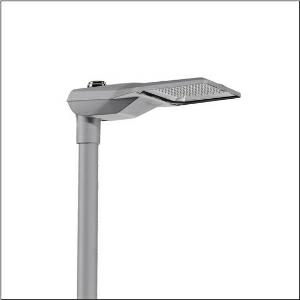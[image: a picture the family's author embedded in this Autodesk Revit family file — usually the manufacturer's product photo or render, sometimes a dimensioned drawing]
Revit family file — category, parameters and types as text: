
# Revit family: streetlight_sl_21_midi___st1_5a_5xe7p47n08mb_d352
name_source: partatom
category: Lighting Fixtures
units: mm (PartAtom-declared; Revit-internal decimal feet)

## family parameters
Cut with Voids When Loaded = No
Host = Face
Light Source = No
Part Type = Normal
Room Calculation Point = No
Round Connector Dimension = Use Diameter
Shared = No

## types (1)
- --- (1 x LED, 19830 lm, 147 W, 4000K)
    Apparent Load = 147 VA
    CIE Flux Codes = 22 53 95 100 100
    Color Rendering = 70
    Color Temperature = 4000K
    Default Elevation = 1800 mm
    Description = Streetlight SL 21 midi, mast luminaire, primary light control with lens, of PMMA, primary optical cover: cover, of toughened safety glass, transparent, light distribution: ST1.5a, light emission: direct distribution, primary light characteristic: asymmetric, installation type: side-entry, LED, 3G 2.5mm², High Power LED, rated luminous flux: 19.830lm, luminous efficacy: 135lm/W, light colour: 740, colour temperature: 4000K, control gear: NEMA (7pin), control: overheat protection, pre-setting: linear dimming characteristic, constant luminous flux control, time-dependent luminous flux control, flexible luminous flux parameterisation, mains connection: 220..240V, AC, 50/60Hz, connection cable pre-assembled, cable length: 12,5m, wiring characteristics: H05VV-F, start of lifetime: 147W, end of service life: 155W, reduction: 65W, luminaire housing, of diecast aluminium (EN AC-44300), powder-coated, Siteco® metallic grey (DB 702S), corrosivity category C5 mid according to DIN EN ISO 12944, multi-level sealing system, sealing non-destructively replaceable, inclination adjustable: 0°, 5°, 10°, 15°, length: 644mm, width: 335mm, height: 110mm, spigot size: 42mm (side-entry), mounting height: 4..8m, protection rating (complete): IP66, insulation class (complete): insulation class I (protective earthing), certification: CE, ENEC, ENEC+, VDE, impact resistance: IK10, permissible operating ambient temperature for outdoor applications: -40..+50°C, standard-compliant lighting for roads and squares, packaging unit: 1 piece

Light Distribution: ST1.5a
    Height = 111 mm
    Lamp = 1 x LED
    Lamp Light Flux = 19830 lm
    Lamp Power = 147 W
    Lamp count = 1
    Length = 644 mm
    Luminous efficacy = 135 lm/W
    Manufacturer = Siteco
    ModVariant = No
    Model = 5XE7P47N08MB
    Number of Poles = 1
    OnlyDefault = Yes
    Power Factor = 1
    Product Name = Streetlight SL 21 midi | ST1.5a
    Product group = mast luminaire | pylon top
    ProductGroupID = 6100
    Protection Class = Protection class I
    Protection Degree = IP 66
    RLX_Detail_Level = 1
    RLX_Emergency_Light_Flux = 0 lm
    RLX_Emergency_Type = 0
    RLX_Emergency_Type_DB = No
    RlxData = <blob elided: 30073 chars, md5=d4ea3021>
    Socket = socket
    Standby Power = 0 W
    System Light Flux = 19830 lm
    System Power = 147 W
    Type Comments = factory setting: luminous flux: 100 % | dim-lin: 254 | 750 mA
    Type Image = l_1294377.jpg
    URL = http://relux.com
    VarID = @adj_154863
    Voltage = 0 V
    Weight = 0.00 kg
    Width = 336 mm

## geometry (parser evidence)
native form markers: Blend x4, Sweep x11
no freeform markers — native parametric forms only
